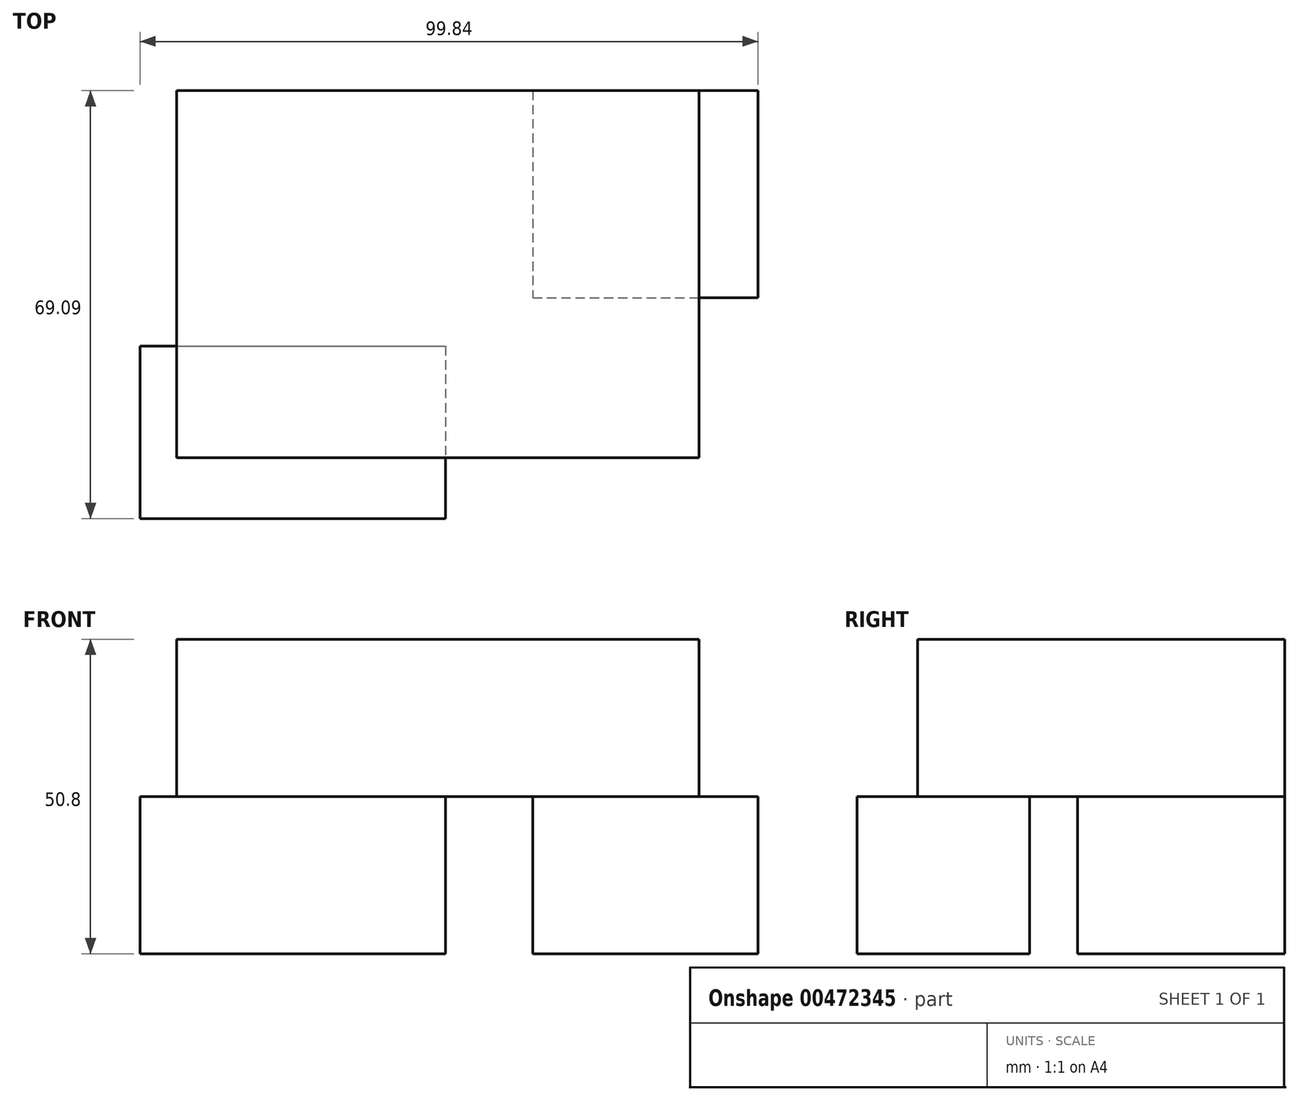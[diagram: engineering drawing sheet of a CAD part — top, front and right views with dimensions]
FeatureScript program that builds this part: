
annotation { "Feature Type Name" : "Feature", "Feature Type Description" : "" }
export const myFeature = defineFeature(function(context is Context, id is Id, definition is map)
    precondition{}
    {
        {
            var Q0;
            Q0=qCreatedBy(makeId("Top.planeOp"),FACE);
            var sketch = newSketch(context, id + "F0", { "sketchPlane" : qUnion([Q0])});
            skLineSegment(sketch, "E0.bottom", {"start": v(0, 0) * mm, "end": v(36.4, 0) * mm});
            skLineSegment(sketch, "E0.top", {"start": v(0, -33.46) * mm, "end": v(36.4, -33.46) * mm});
            skLineSegment(sketch, "E0.left", {"start": v(0, 0) * mm, "end": v(0, -33.46) * mm});
            skLineSegment(sketch, "E0.right", {"start": v(36.4, 0) * mm, "end": v(36.4, -33.46) * mm});
            skSolve(sketch);
        }
        {
            var Q0;
            Q0 = qSketchRegion(id + "F0", true);
            extrude(context, id + "F1", {"entities" : qUnion([Q0]), "depth" : 25.4 * mm});
        }
        {
            var Q0;
            Q0=qCreatedBy(makeId("Top.planeOp"),FACE);
            var sketch = newSketch(context, id + "F2", { "sketchPlane" : qUnion([Q0])});
            skLineSegment(sketch, "E1.bottom", {"start": v(-63.44, -41.24) * mm, "end": v(-14.12, -41.24) * mm});
            skLineSegment(sketch, "E1.top", {"start": v(-63.44, -69.1) * mm, "end": v(-14.12, -69.1) * mm});
            skLineSegment(sketch, "E1.left", {"start": v(-63.44, -41.24) * mm, "end": v(-63.44, -69.1) * mm});
            skLineSegment(sketch, "E1.right", {"start": v(-14.12, -41.24) * mm, "end": v(-14.12, -69.1) * mm});
            skSolve(sketch);
        }
        {
            var Q0;
            Q0 = qSketchRegion(id + "F2", true);
            extrude(context, id + "F3", {"entities" : qUnion([Q0]), "depth" : 25.4 * mm});
        }
        {
            var Q0;
            Q0=qCreatedBy(makeId("Top.planeOp"),FACE);
            cPlane(context, id + "F4", {"entities" : qUnion([Q0]), "cplaneType" : CPlaneType.OFFSET, "offset" : 25.4 * mm, "width" : 152.4 * mm, "height" : 152.4 * mm});
        }
        {
            var Q0;
            Q0=qCreatedBy(id+"F4.planeOp",FACE);
            var sketch = newSketch(context, id + "F5", { "sketchPlane" : qUnion([Q0])});
            skLineSegment(sketch, "E2.bottom", {"start": v(-57.53, 0) * mm, "end": v(26.85, 0) * mm});
            skLineSegment(sketch, "E2.top", {"start": v(-57.53, -59.3) * mm, "end": v(26.85, -59.3) * mm});
            skLineSegment(sketch, "E2.left", {"start": v(-57.53, 0) * mm, "end": v(-57.53, -59.3) * mm});
            skLineSegment(sketch, "E2.right", {"start": v(26.85, 0) * mm, "end": v(26.85, -59.3) * mm});
            skSolve(sketch);
        }
        {
            var Q0;
            Q0 = qSketchRegion(id + "F5", true);
            extrude(context, id + "F6", {"entities" : qUnion([Q0]), "depth" : 25.4 * mm});
        }
    });
